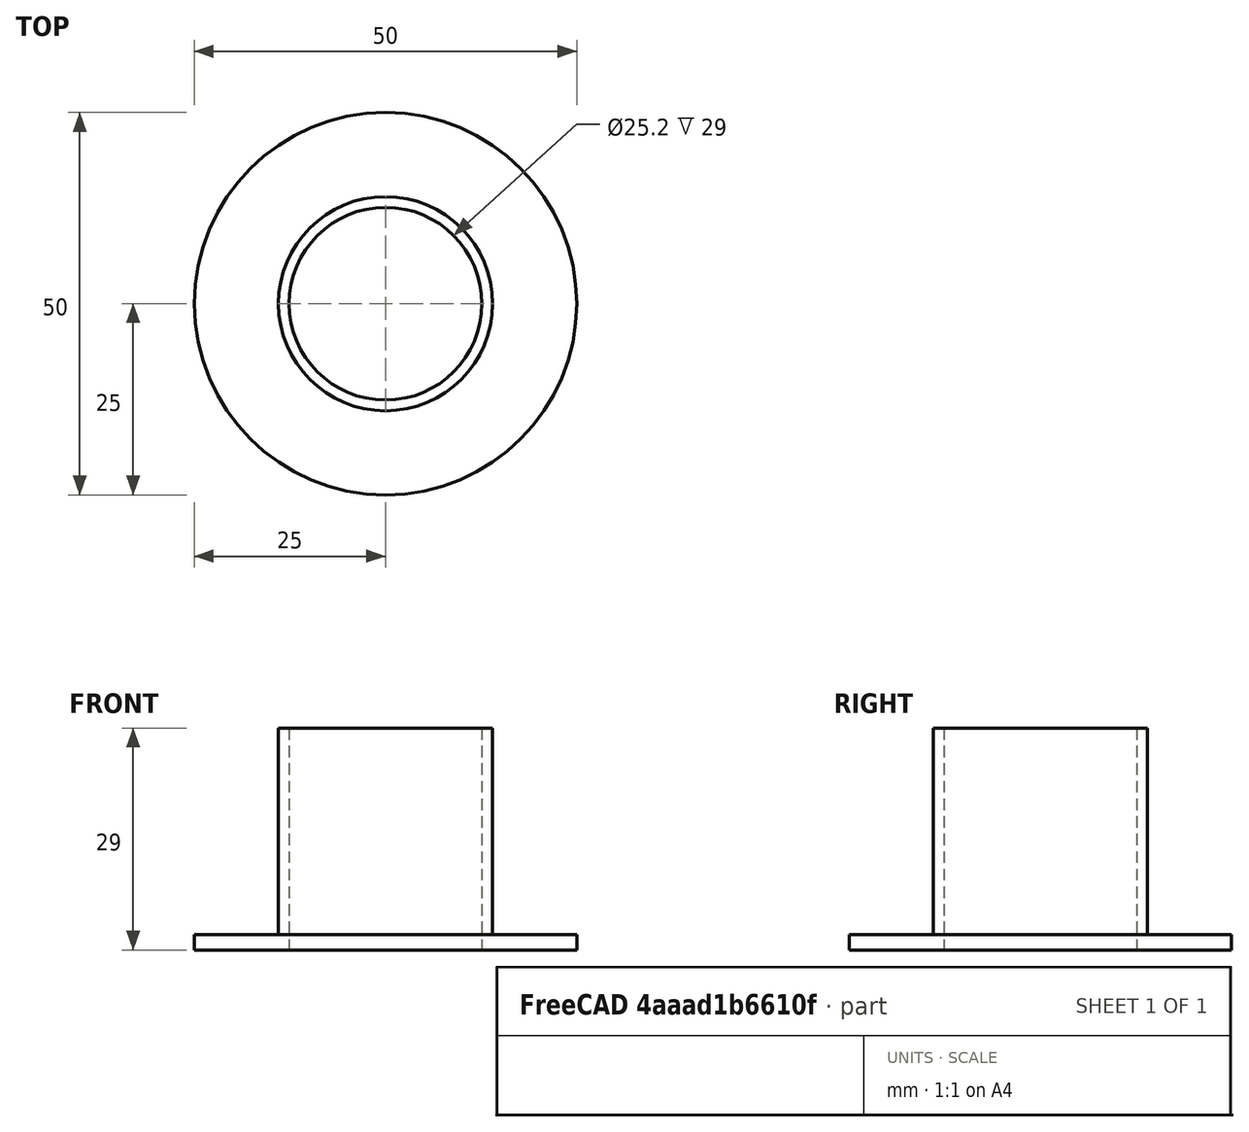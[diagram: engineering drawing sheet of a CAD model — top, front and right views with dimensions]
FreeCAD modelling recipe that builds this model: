
FCSTD DOCUMENT  (FreeCAD 0.19R24267 +148 (Git))
Label: BT50 Tube Cutter Guide
License: All rights reserved
LicenseURL: http://en.wikipedia.org/wiki/All_rights_reserved
objects: Sketcher::SketchObject×2, PartDesign::Pad×2, PartDesign::Hole×1, PartDesign::Body×1
note: 9 computed .brp shape members not serialized (recipe doc carries the construction recipe); baked Part::Feature solids carry a one-line shape summary decoded from their .brp

FEATURE [Sketcher::SketchObject] Sketch
  FullyConstrained = true
  MapMode = 5
  Support = -> [XY_Plane]
  sketch-geometry (1):
    g0: Circle CenterX=0 CenterY=0 CenterZ=0 NormalX=0 NormalY=0 NormalZ=1 AngleXU=0 Radius=25
  constraints (2):
    c: Coincident(g0,g-1)
    c: Diameter(g0) = 50
FEATURE [PartDesign::Pad] Pad
  Direction = (1,1,1)
  Length = 2
  Length2 = 100
  Profile = -> Sketch
  Type = 0
FEATURE [Sketcher::SketchObject] Sketch001
  FullyConstrained = false
  MapMode = 5
  Support = -> [XY_Plane]
  sketch-geometry (1):
    g0: Circle CenterX=0 CenterY=0 CenterZ=0 NormalX=0 NormalY=0 NormalZ=1 AngleXU=0 Radius=14
  constraints (1):
    c: Diameter(g0) = 28
FEATURE [PartDesign::Pad] Pad001
  BaseFeature = -> Pad
  Direction = (1,1,1)
  Length = 29
  Length2 = 100
  Profile = -> Sketch001
  Type = 0
FEATURE [PartDesign::Hole] Hole
  BaseFeature = -> Pad001
  Depth = 31
  DepthType = 0
  Diameter = 25.2
  DrillForDepth = false
  DrillPoint = 1
  DrillPointAngle = 118
  HoleCutCountersinkAngle = 90
  HoleCutCustomValues = false
  HoleCutDepth = 0
  HoleCutDiameter = 0
  HoleCutType = 0
  ModelActualThread = false
  Profile = -> Pad001 [Face6]
  Tapered = false
  TaperedAngle = 90
  ThreadAngle = 0
  ThreadClass = 0
  ThreadCutOffInner = 0
  ThreadCutOffOuter = 0
  ThreadDirection = 0
  ThreadFit = 0
  ThreadPitch = 0
  ThreadSize = 0
  ThreadType = 0
  Threaded = false
FEATURE [PartDesign::Body] Body
  Group = -> [Sketch,Pad,Sketch001,Pad001,Hole]
  Origin = -> Origin
  Tip = -> Hole
